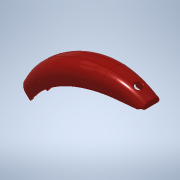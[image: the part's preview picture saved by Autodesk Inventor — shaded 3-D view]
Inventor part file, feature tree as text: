
AUTODESK INVENTOR PART (.ipt)
format: ipt  version: 2020 (Build 240168000, 168)  size: 8,020,480 bytes
history: native  units: in
note: dims shown in document units (in); Inventor stores cm internally (conversion verified against a paired STEP export)
features: fillet x14, sketch x12, extrude x10, delete_face x4, revolve x4, other x3, sweep x1, draft x1, mirror x1, boolean_combine x1, chamfer x1, split x1
ambient origin geometry x8: Origin, YZ Plane, XZ Plane, XY Plane, X Axis, Y Axis, Z Axis, Center Point
bodies: Solid5 (feature_tree), Solid6 (feature_tree)
feature tree (53):
  other  "Part1b1.ipt"
  extrude  "Extrusion1"  Depth=1.1in
  sketch  "Sketch3-<F>"  dims[d7=0.78in d8=1.1in]
  sketch  "Sketch6-<F>"  dims[d10=1.0in d13=2.75in d14=0.975in d15=0.26in d16=0.405in d17=0.725in]
  sketch  "3D Sketch2"
  sweep  "Sweep3"
  delete_face  "Delete Face22"
  delete_face  "Delete Face23"
  draft  "FaceDraft1"
  mirror  "Mirror2"
  fillet  "Fillet12"  Radius=0.975in
  fillet  "Fillet13"  Radius=0.26in
  delete_face  "Delete Face24"
  delete_face  "Delete Face25"
  fillet  "Fillet14"  Radius=0.405in
  fillet  "Fillet15"  Radius=0.725in
  extrude  "Extrusion2"  Depth=2.695in
  fillet  "Fillet16"  Radius=0.268in
  fillet  "Fillet17"  Radius=0.12in
  fillet  "Fillet18"  Radius=0.3in
  boolean_combine  "Combine3"
  extrude  "Extrusion5"  Depth=1.035in
  fillet  "Fillet19"  Radius=0.18in
  sketch  "Sketch8-<F>"  dims[d18=0.625in d19=2.695in d20=0.268in d21=0.12in d22=0.3in d23=-0.0687in]
  extrude  "Extrusion3"  Depth=0.7in
  extrude  "Extrusion4"  Depth=1.15in
  chamfer  "Chamfer1"  Distance=0.145in
  sketch  "Sketch11-<F>"  dims[d25=0.78in d26=1.035in d30=0.18in]
  extrude  "Extrusion6"  Depth=0.01in
  fillet  "Fillet21"  Radius=0.09in
  extrude  "Extrusion7"  Depth=0.01in
  fillet  "Fillet25"  Radius=0.35in
  fillet  "Fillet26"  Radius=0.75in
  fillet  "Fillet22"  Radius=0.075in
  split  "Split2"
  sketch  "Sketch14-<F>"  dims[d31=0.475in d32=0.7in]
  revolve  "Revolution1"  [1 undecoded]
  revolve  "Revolution2"  [1 undecoded]
  revolve  "Revolution3"  [1 undecoded]
  revolve  "Revolution4"  [1 undecoded]
  fillet  "Fillet24"  Radius=0.03in
  sketch  "Sketch15-<F>"  dims[d33=0.975in d34=1.15in]
  extrude  "Extrusion11"  Depth=0.01in
  extrude  "Extrusion12"  Depth=0.01in
  fillet  "Fillet23"  Radius=0.225in
  extrude  "Extrusion13"  Depth=0.01in
  sketch  "Sketch2-<F>"  dims[d35=1.3in]
  sketch  "Sketch7-<F>"  dims[d36=0.1in]
  other  "Solid1::Part1b1.ipt"
  other  "TaggingFeature1"
  sketch  "Sketch9-<F>"  dims[d37=0.112in]
  sketch  "Sketch10-<F>"  dims[d38=0.14in]
  sketch  "Sketch16-<F>"  dims[d39=0.15in d40=0.145in d41=0.125in d42=0.09in d53=0.0412in d54=0.35in d55=0.75in d56=0.075in d57=0.425in d58=0.0in d59=0.0in d60=0.4947in d61=0.375in d62=0.03in d63=0.065in d107=0.0687in d108=0.225in d109=0.5in d110=0.625in d111=0.3937in d112=0.64in d113=0.0in d114=0.45in d115=0.1969in d116=0.7in d117=0.1969in d118=0.475in d119=0.3in d120=0.55in d121=0.1722in d122=0.08in d123=0.06in d124=0.125in d125=0.3937in d126=0.08in d127=0.06in d128=0.125in d129=0.3937in d130=0.045in d131=0.09in d132=0.115in d133=0.2461in d134=0.045in d135=0.09in d136=0.115in d137=0.2541in d139=0.052in d140=0.06in d141=0.198in d142=0.2554in d143=0.0in d144=0.008in d145=0.02in d146=0.03in d147=0.143in d148=0.1755in d149=0.023in d150=0.1in d151=0.008in d152=0.125in d153=0.108in d154=0.03in d155=0.3937in d156=0.101in d157=1.0in d158=0.0in d159=0.136in d160=0.0in d161=0.019in d162=0.016in d163=45.0deg d167=1.1501in d168=0.268in d169=1.512in d170=0.5in d171=0.7in d172=0.03in d173=0.03in d174=0.03in d175=0.166in d176=0.0in d177=0.01in d178=0.198in d179=0.2745in d180=0.5in d184=0.2752in d185=0.0in d187=0.0118in d188=0.0in d198=0.008in d199=0.008in d209=0.009in d210=0.009in d231=0.327in d232=1.264in d233=0.1271in d234=0.2474in d237=0.01in d238=0.01in d239=0.25in d240=90.0deg d241=90.0deg d242=0.1465in d243=0.055in d244=0.04in d245=0.03in d246=0.052in d247=0.1168in d248=0.04in d249=0.024in d250=0.052in d251=0.1168in d252=90.0deg d253=90.0deg d254=0.317in d255=0.237in d256=0.0363in d257=1.0915in d258=0.0225in d259=0.1571in d260=0.0in d261=0.075in d262=0.045in d263=0.235in d264=0.0in d265=0.01in d266=0.03in d267=0.0in d268=0.7578in d269=0.15in d270=0.0748in d271=0.0748in d273=0.0787in d274=0.189in d278=0.0098in d284=0.2559in d285=0.0276in d286=0.0in d287=0.1535in d288=0.0374in d289=0.0079in d290=0.0059in]
note: 4 required parameter values undecoded (feature->parameter linkage not recoverable at this tier; creation-order binding heuristic only, values carry confidence <= 0.55)
